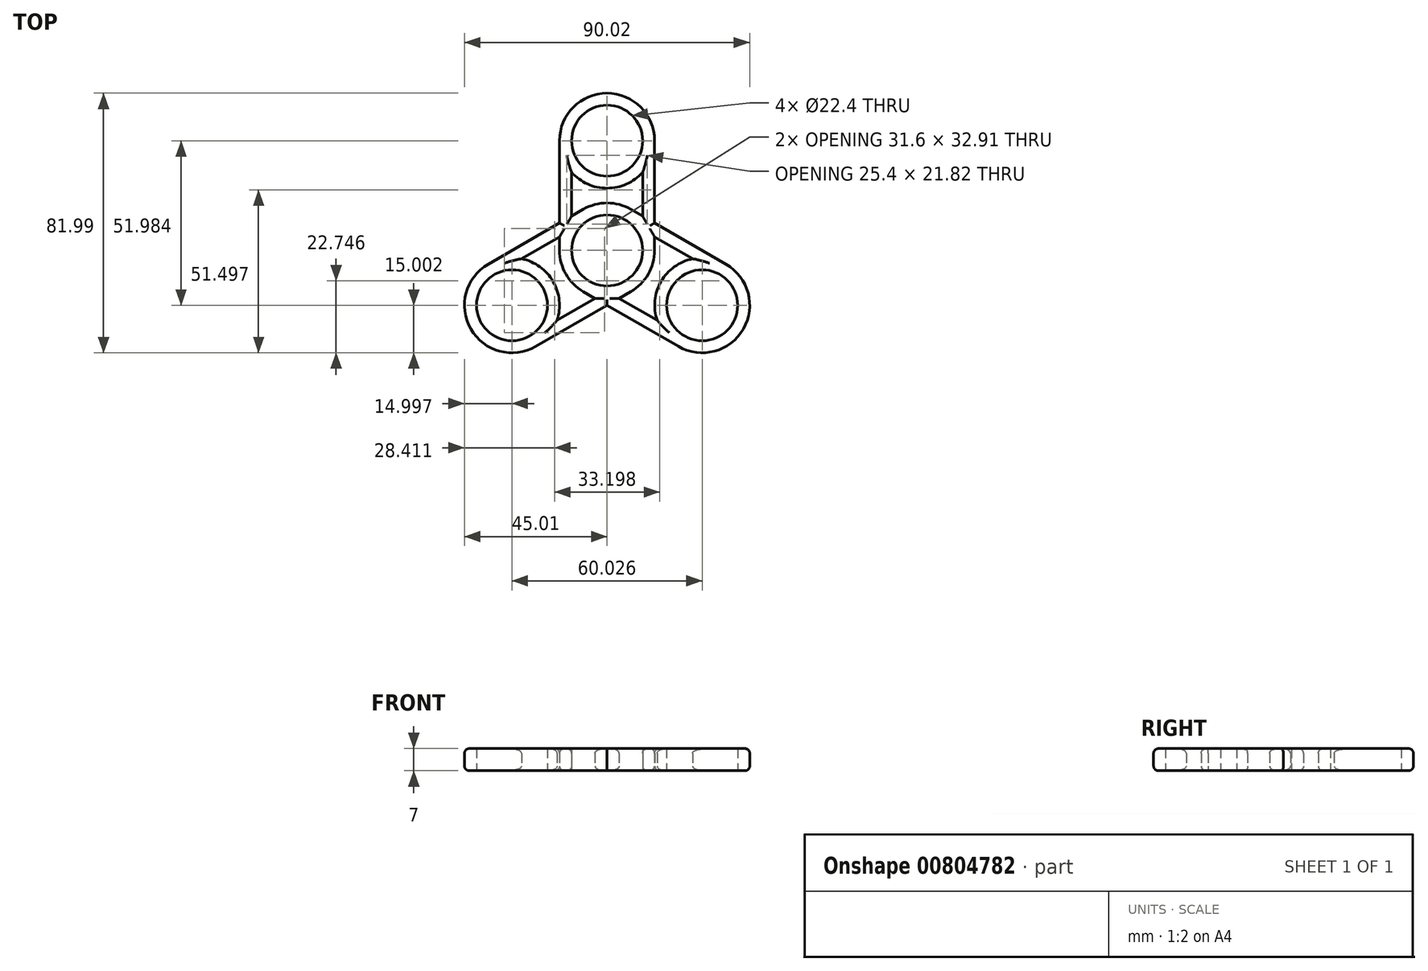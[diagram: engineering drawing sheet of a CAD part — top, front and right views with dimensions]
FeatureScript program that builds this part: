
annotation { "Feature Type Name" : "Feature", "Feature Type Description" : "" }
export const myFeature = defineFeature(function(context is Context, id is Id, definition is map)
    precondition{}
    {
        {
            var Q0;
            Q0=qCreatedBy(makeId("Top.planeOp"),FACE);
            var sketch = newSketch(context, id + "F0", { "sketchPlane" : qUnion([Q0])});
            skCircle(sketch, "E0", {"center": v(0, 0) * mm, "radius": 11.2 * mm});
            skArc(sketch, "E1", {"start": v(-15, 0) * mm, "mid": v(-13, -7.5) * mm, "end": v(-7.5, -13) * mm});
            skCircle(sketch, "E2", {"center": v(0, 34.66) * mm, "radius": 11.2 * mm});
            skArc(sketch, "E3", {"start": v(-11.2, 24.68) * mm, "mid": v(0, 19.66) * mm, "end": v(11.2, 24.68) * mm});
            skCircle(sketch, "E4.1.0", {"center": v(-30.01, -17.33) * mm, "radius": 11.2 * mm});
            skArc(sketch, "E4.1.1", {"start": v(-37.51, -4.34) * mm, "mid": v(-43, -24.83) * mm, "end": v(-22.51, -30.32) * mm});
            skCircle(sketch, "E4.2.0", {"center": v(30.01, -17.33) * mm, "radius": 11.2 * mm});
            skArc(sketch, "E4.2.1", {"start": v(22.51, -30.32) * mm, "mid": v(43, -24.83) * mm, "end": v(37.51, -4.34) * mm});
            skLineSegment(sketch, "E5", {"start": v(15, 34.66) * mm, "end": v(15, 8.66) * mm});
            skLineSegment(sketch, "E6", {"start": v(0, 34.66) * mm, "end": v(11.2, 34.66) * mm});
            skLineSegment(sketch, "E7", {"start": v(11.2, 24.68) * mm, "end": v(11.2, 10.85) * mm});
            skLineSegment(sketch, "E8", {"start": v(0, 34.66) * mm, "end": v(-11.2, 34.66) * mm});
            skLineSegment(sketch, "E9", {"start": v(-11.2, 24.68) * mm, "end": v(-11.2, 10.85) * mm});
            skLineSegment(sketch, "E10", {"start": v(-15, 34.66) * mm, "end": v(-15, 8.66) * mm});
            skLineSegment(sketch, "E11.1.0", {"start": v(-37.51, -4.34) * mm, "end": v(-15, 8.66) * mm});
            skLineSegment(sketch, "E11.1.1", {"start": v(-26.97, -2.64) * mm, "end": v(-15, 4.27) * mm});
            skLineSegment(sketch, "E11.1.2", {"start": v(-22.51, -30.32) * mm, "end": v(0, -17.32) * mm});
            skLineSegment(sketch, "E11.1.3", {"start": v(-15.77, -22.04) * mm, "end": v(-3.8, -15.13) * mm});
            skLineSegment(sketch, "E11.2.0", {"start": v(22.51, -30.32) * mm, "end": v(0, -17.32) * mm});
            skLineSegment(sketch, "E11.2.1", {"start": v(15.77, -22.04) * mm, "end": v(3.8, -15.13) * mm});
            skLineSegment(sketch, "E11.2.2", {"start": v(37.51, -4.34) * mm, "end": v(15, 8.66) * mm});
            skLineSegment(sketch, "E11.2.3", {"start": v(26.97, -2.64) * mm, "end": v(15, 4.27) * mm});
            skArc(sketch, "E12.trimOffspring", {"start": v(15, 34.66) * mm, "mid": v(0, 49.66) * mm, "end": v(-15, 34.66) * mm});
            skLineSegment(sketch, "E13.trimOffspring", {"start": v(-11.2, 10.85) * mm, "end": v(-7.5, 13) * mm});
            skLineSegment(sketch, "E14.trimOffspring", {"start": v(-15, 4.27) * mm, "end": v(-15, 0) * mm});
            skPoint(sketch, "E15.orphan", {"position": v(-35.61, -7.63) * mm});
            skPoint(sketch, "E16.orphan", {"position": v(-24.41, -27.03) * mm});
            skArc(sketch, "E17.trimOffspring", {"start": v(-15.77, -22.04) * mm, "mid": v(-17.02, -9.83) * mm, "end": v(-26.97, -2.64) * mm});
            skArc(sketch, "E18.trimOffspring", {"start": v(7.5, -13) * mm, "mid": v(13, -7.5) * mm, "end": v(15, 0) * mm});
            skLineSegment(sketch, "E19.trimOffspring", {"start": v(-3.8, -15.13) * mm, "end": v(-7.5, -13) * mm});
            skLineSegment(sketch, "E20.trimOffspring", {"start": v(3.8, -15.13) * mm, "end": v(7.5, -13) * mm});
            skPoint(sketch, "E21.orphan", {"position": v(24.41, -27.03) * mm});
            skPoint(sketch, "E22.orphan", {"position": v(35.61, -7.63) * mm});
            skArc(sketch, "E23.trimOffspring", {"start": v(26.97, -2.64) * mm, "mid": v(17.02, -9.83) * mm, "end": v(15.77, -22.04) * mm});
            skLineSegment(sketch, "E24.trimOffspring", {"start": v(15, 4.27) * mm, "end": v(15, 0) * mm});
            skArc(sketch, "E25.trimOffspring", {"start": v(7.5, 13) * mm, "mid": v(0, 15) * mm, "end": v(-7.5, 13) * mm});
            skLineSegment(sketch, "E26.trimOffspring", {"start": v(11.2, 10.85) * mm, "end": v(7.5, 13) * mm});
            skPoint(sketch, "E27.trimOffspring.end.orphan", {"position": v(-11.2, 0) * mm});
            skPoint(sketch, "E28.trimOffspring.end.orphan", {"position": v(11.2, 0) * mm});
            skSolve(sketch);
        }
        {
            var Q0;
            Q0=makeQuery(id+"F0.imprint","IMPRINT",FACE,{"disambiguationData":[TD([[makeQuery(id+"F0.imprint","IMPRINT",EDGE,{"derivedFrom":sQuery(id+"F0.wireOp",EDGE,"E0")}),-1.0]])]});
            extrude(context, id + "F1", {"entities" : qUnion([Q0]), "depth" : 7 * mm, "offsetDistance" : 25 * mm});
        }
        {
            var Q0;
            Q0=makeQuery(id+"F1.opExtrude","CAP_EDGE",EDGE,{"disambiguationData":[OSD([sQuery(id+"F0.wireOp",EDGE,"E10")])],"isStart":false});
            var Q1;
            Q1=makeQuery(id+"F1.opExtrude","CAP_EDGE",EDGE,{"disambiguationData":[OSD([sQuery(id+"F0.wireOp",EDGE,"E11.1.0")])],"isStart":false});
            var Q2;
            Q2=makeQuery(id+"F1.opExtrude","CAP_EDGE",EDGE,{"disambiguationData":[OSD([sQuery(id+"F0.wireOp",EDGE,"E11.2.0")])],"isStart":false});
            var Q3;
            Q3=makeQuery(id+"F1.opExtrude","CAP_EDGE",EDGE,{"disambiguationData":[OSD([sQuery(id+"F0.wireOp",EDGE,"E5")])],"isStart":true});
            var Q4;
            Q4=makeQuery(id+"F1.opExtrude","CAP_EDGE",EDGE,{"disambiguationData":[OSD([sQuery(id+"F0.wireOp",EDGE,"E11.2.2")])],"isStart":true});
            var Q5;
            Q5=makeQuery(id+"F1.opExtrude","CAP_EDGE",EDGE,{"disambiguationData":[OSD([sQuery(id+"F0.wireOp",EDGE,"E11.1.2")])],"isStart":true});
            fillet(context, id + "F2", {"entities" : qUnion([Q0, Q1, Q2, Q3, Q4, Q5]), "radius" : 1.5 * mm, "tangentPropagation" : true, "allowEdgeOverflow" : false});
        }
        {
            var Q0;
            Q0=makeQuery(id+"F1.opExtrude","CAP_EDGE",EDGE,{"disambiguationData":[OSD([sQuery(id+"F0.wireOp",EDGE,"E23.trimOffspring")])],"isStart":false});
            var Q1;
            Q1=makeQuery(id+"F1.opExtrude","CAP_EDGE",EDGE,{"disambiguationData":[OSD([sQuery(id+"F0.wireOp",EDGE,"E11.2.1")])],"isStart":false});
            var Q2;
            Q2=makeQuery(id+"F1.opExtrude","CAP_EDGE",EDGE,{"disambiguationData":[OSD([sQuery(id+"F0.wireOp",EDGE,"E11.2.3")])],"isStart":false});
            var Q3;
            Q3=makeQuery(id+"F1.opExtrude","CAP_EDGE",EDGE,{"disambiguationData":[OSD([sQuery(id+"F0.wireOp",EDGE,"E18.trimOffspring")])],"isStart":false});
            var Q4;
            Q4=makeQuery(id+"F1.opExtrude","CAP_EDGE",EDGE,{"disambiguationData":[OSD([sQuery(id+"F0.wireOp",EDGE,"E20.trimOffspring")])],"isStart":false});
            var Q5;
            Q5=makeQuery(id+"F1.opExtrude","CAP_EDGE",EDGE,{"disambiguationData":[OSD([sQuery(id+"F0.wireOp",EDGE,"E24.trimOffspring")])],"isStart":false});
            var Q6;
            Q6=makeQuery(id+"F1.opExtrude","CAP_EDGE",EDGE,{"disambiguationData":[OSD([sQuery(id+"F0.wireOp",EDGE,"E11.1.1")])],"isStart":false});
            var Q7;
            Q7=makeQuery(id+"F1.opExtrude","CAP_EDGE",EDGE,{"disambiguationData":[OSD([sQuery(id+"F0.wireOp",EDGE,"E17.trimOffspring")])],"isStart":false});
            var Q8;
            Q8=makeQuery(id+"F1.opExtrude","CAP_EDGE",EDGE,{"disambiguationData":[OSD([sQuery(id+"F0.wireOp",EDGE,"E11.1.3")])],"isStart":false});
            var Q9;
            Q9=makeQuery(id+"F1.opExtrude","CAP_EDGE",EDGE,{"disambiguationData":[OSD([sQuery(id+"F0.wireOp",EDGE,"E1")])],"isStart":false});
            var Q10;
            Q10=makeQuery(id+"F1.opExtrude","CAP_EDGE",EDGE,{"disambiguationData":[OSD([sQuery(id+"F0.wireOp",EDGE,"E19.trimOffspring")])],"isStart":false});
            var Q11;
            Q11=makeQuery(id+"F1.opExtrude","CAP_EDGE",EDGE,{"disambiguationData":[OSD([sQuery(id+"F0.wireOp",EDGE,"E14.trimOffspring")])],"isStart":false});
            var Q12;
            Q12=makeQuery(id+"F1.opExtrude","CAP_EDGE",EDGE,{"disambiguationData":[OSD([sQuery(id+"F0.wireOp",EDGE,"E3")])],"isStart":false});
            var Q13;
            Q13=makeQuery(id+"F1.opExtrude","CAP_EDGE",EDGE,{"disambiguationData":[OSD([sQuery(id+"F0.wireOp",EDGE,"E9")])],"isStart":false});
            var Q14;
            Q14=makeQuery(id+"F1.opExtrude","CAP_EDGE",EDGE,{"disambiguationData":[OSD([sQuery(id+"F0.wireOp",EDGE,"E7")])],"isStart":false});
            var Q15;
            Q15=makeQuery(id+"F1.opExtrude","CAP_EDGE",EDGE,{"disambiguationData":[OSD([sQuery(id+"F0.wireOp",EDGE,"E25.trimOffspring")])],"isStart":false});
            var Q16;
            Q16=makeQuery(id+"F1.opExtrude","CAP_EDGE",EDGE,{"disambiguationData":[OSD([sQuery(id+"F0.wireOp",EDGE,"E26.trimOffspring")])],"isStart":false});
            var Q17;
            Q17=makeQuery(id+"F1.opExtrude","CAP_EDGE",EDGE,{"disambiguationData":[OSD([sQuery(id+"F0.wireOp",EDGE,"E13.trimOffspring")])],"isStart":false});
            fillet(context, id + "F3", {"entities" : qUnion([Q0, Q1, Q2, Q3, Q4, Q5, Q6, Q7, Q8, Q9, Q10, Q11, Q12, Q13, Q14, Q15, Q16, Q17]), "radius" : 1.5 * mm, "tangentPropagation" : true, "allowEdgeOverflow" : false});
        }
        {
            var Q0;
            Q0=makeQuery(id+"F1.opExtrude","CAP_EDGE",EDGE,{"disambiguationData":[OSD([sQuery(id+"F0.wireOp",EDGE,"E17.trimOffspring")])],"isStart":true});
            var Q1;
            Q1=makeQuery(id+"F1.opExtrude","CAP_EDGE",EDGE,{"disambiguationData":[OSD([sQuery(id+"F0.wireOp",EDGE,"E11.1.3")])],"isStart":true});
            var Q2;
            Q2=makeQuery(id+"F1.opExtrude","CAP_EDGE",EDGE,{"disambiguationData":[OSD([sQuery(id+"F0.wireOp",EDGE,"E11.1.1")])],"isStart":true});
            var Q3;
            Q3=makeQuery(id+"F1.opExtrude","CAP_EDGE",EDGE,{"disambiguationData":[OSD([sQuery(id+"F0.wireOp",EDGE,"E9")])],"isStart":true});
            var Q4;
            Q4=makeQuery(id+"F1.opExtrude","CAP_EDGE",EDGE,{"disambiguationData":[OSD([sQuery(id+"F0.wireOp",EDGE,"E3")])],"isStart":true});
            var Q5;
            Q5=makeQuery(id+"F1.opExtrude","CAP_EDGE",EDGE,{"disambiguationData":[OSD([sQuery(id+"F0.wireOp",EDGE,"E7")])],"isStart":true});
            var Q6;
            Q6=makeQuery(id+"F1.opExtrude","CAP_EDGE",EDGE,{"disambiguationData":[OSD([sQuery(id+"F0.wireOp",EDGE,"E23.trimOffspring")])],"isStart":true});
            var Q7;
            Q7=makeQuery(id+"F1.opExtrude","CAP_EDGE",EDGE,{"disambiguationData":[OSD([sQuery(id+"F0.wireOp",EDGE,"E11.2.3")])],"isStart":true});
            var Q8;
            Q8=makeQuery(id+"F1.opExtrude","CAP_EDGE",EDGE,{"disambiguationData":[OSD([sQuery(id+"F0.wireOp",EDGE,"E11.2.1")])],"isStart":true});
            var Q9;
            Q9=makeQuery(id+"F1.opExtrude","CAP_EDGE",EDGE,{"disambiguationData":[OSD([sQuery(id+"F0.wireOp",EDGE,"E1")])],"isStart":true});
            var Q10;
            Q10=makeQuery(id+"F1.opExtrude","CAP_EDGE",EDGE,{"disambiguationData":[OSD([sQuery(id+"F0.wireOp",EDGE,"E19.trimOffspring")])],"isStart":true});
            var Q11;
            Q11=makeQuery(id+"F1.opExtrude","CAP_EDGE",EDGE,{"disambiguationData":[OSD([sQuery(id+"F0.wireOp",EDGE,"E14.trimOffspring")])],"isStart":true});
            var Q12;
            Q12=makeQuery(id+"F1.opExtrude","CAP_EDGE",EDGE,{"disambiguationData":[OSD([sQuery(id+"F0.wireOp",EDGE,"E13.trimOffspring")])],"isStart":true});
            var Q13;
            Q13=makeQuery(id+"F1.opExtrude","CAP_EDGE",EDGE,{"disambiguationData":[OSD([sQuery(id+"F0.wireOp",EDGE,"E25.trimOffspring")])],"isStart":true});
            var Q14;
            Q14=makeQuery(id+"F1.opExtrude","CAP_EDGE",EDGE,{"disambiguationData":[OSD([sQuery(id+"F0.wireOp",EDGE,"E26.trimOffspring")])],"isStart":true});
            var Q15;
            Q15=makeQuery(id+"F1.opExtrude","CAP_EDGE",EDGE,{"disambiguationData":[OSD([sQuery(id+"F0.wireOp",EDGE,"E24.trimOffspring")])],"isStart":true});
            var Q16;
            Q16=makeQuery(id+"F1.opExtrude","CAP_EDGE",EDGE,{"disambiguationData":[OSD([sQuery(id+"F0.wireOp",EDGE,"E18.trimOffspring")])],"isStart":true});
            var Q17;
            Q17=makeQuery(id+"F1.opExtrude","CAP_EDGE",EDGE,{"disambiguationData":[OSD([sQuery(id+"F0.wireOp",EDGE,"E20.trimOffspring")])],"isStart":true});
            fillet(context, id + "F4", {"entities" : qUnion([Q0, Q1, Q2, Q3, Q4, Q5, Q6, Q7, Q8, Q9, Q10, Q11, Q12, Q13, Q14, Q15, Q16, Q17]), "radius" : 1.5 * mm, "tangentPropagation" : true, "allowEdgeOverflow" : false});
        }
    });
